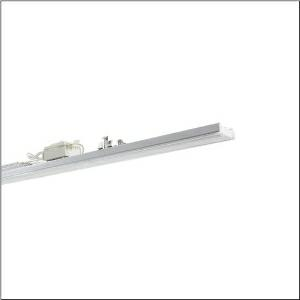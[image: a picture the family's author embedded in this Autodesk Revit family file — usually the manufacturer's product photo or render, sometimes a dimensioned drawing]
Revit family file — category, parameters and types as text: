
# Revit family: licross_r__21_recessed_ho_52tl12dn4fxm3s_7ef7
name_source: partatom
category: Lighting Fixtures
units: mm (PartAtom-declared; Revit-internal decimal feet)

## family parameters
Cut with Voids When Loaded = No
Host = Face
Light Source = No
Part Type = Normal
Room Calculation Point = No
Round Connector Dimension = Use Diameter
Shared = No

## types (1)
- --- (1 x LED, 930 lm, 7.5 W, 4000K)
    Apparent Load = 8 VA
    CIE Flux Codes = 69 91 98 100 100
    Color Rendering = 80
    Color Temperature = 4000K
    Default Elevation = 1800 mm
    Description = Licross® 21 Recessed HO, luminaire insert, of sheet steel, galvanised, coil coated, white, length: 1.500mm, width: 66mm, height: 67mm, LED rated luminous flux: 15.000lm, light colour: 840, control gear: DALI 2 (for two DALI lines), with plug, 6-pole, with phase selection, for trunking rail, 14-core, mains connection: 220..240V, AC, 50/60Hz, rated input power: 88W, halogen-free wiring, for emergency light function, for trunking rail, 14-core, converter,control gear: single battery element, battery: LiFePO4, 9Ah, primary optical cover: cover, of PMMA, light emission: direct distribution, primary light characteristic: symmetric, protection rating (complete): IP40, insulation class (complete): insulation class I (protective earthing), certification: CE, UKCA, protection symbol: D if used in an environment without relevant dust loads with corresponding accessories, impact resistance: IK06, permissible ambient temperature for indoor applications: +5..+30°C, standard: EN 60598-2-22, LABS conformity tested according to VDMA 24364:2018-05, reducing of maximum allowable ambient temperature of 5°C with ceiling mounting, corresponds to IFS (International Featured Standards) requirements for safety and quality in the food industry, packaging unit: 1 piece
    Height = 58 mm
    Lamp = 1 x LED
    Lamp Light Flux = 930 lm
    Lamp Power = 7.5 W
    Lamp count = 1
    Length = 1500 mm
    Luminous efficacy = 124 lm/W
    Manufacturer = Siteco
    ModVariant = No
    Model = 52TL12DN4FXM3S
    Mounting Place = Ceiling
    Mounting Type = Pendant
    Number of Poles = 1
    OnlyDefault = Yes
    Power Factor = 1
    Product Name = Licross® 21 Recessed HO
    Product group = luminaire insert
    ProductGroupID = 902
    Protection Class = Protection class I
    Protection Degree = IP 40
    RLX_Detail_Level = 1
    RLX_Emergency_Light_Flux = 0 lm
    RLX_Emergency_Type = 0
    RLX_Emergency_Type_DB = No
    RlxData = <blob elided: 25073 chars, md5=4a51c02e>
    Socket = socket
    Standby Power = 0 W
    System Light Flux = 930 lm
    System Power = 8 W
    Type Comments = : emergency light operation: 3 h
    Type Image = l_1296930.jpg
    URL = http://relux.com
    VarID = @adj_109324
    Voltage = 0 V
    Weight = 0.00 kg
    Width = 66 mm

## geometry (parser evidence)
native form markers: Blend x4, Sweep x10
no freeform markers — native parametric forms only
